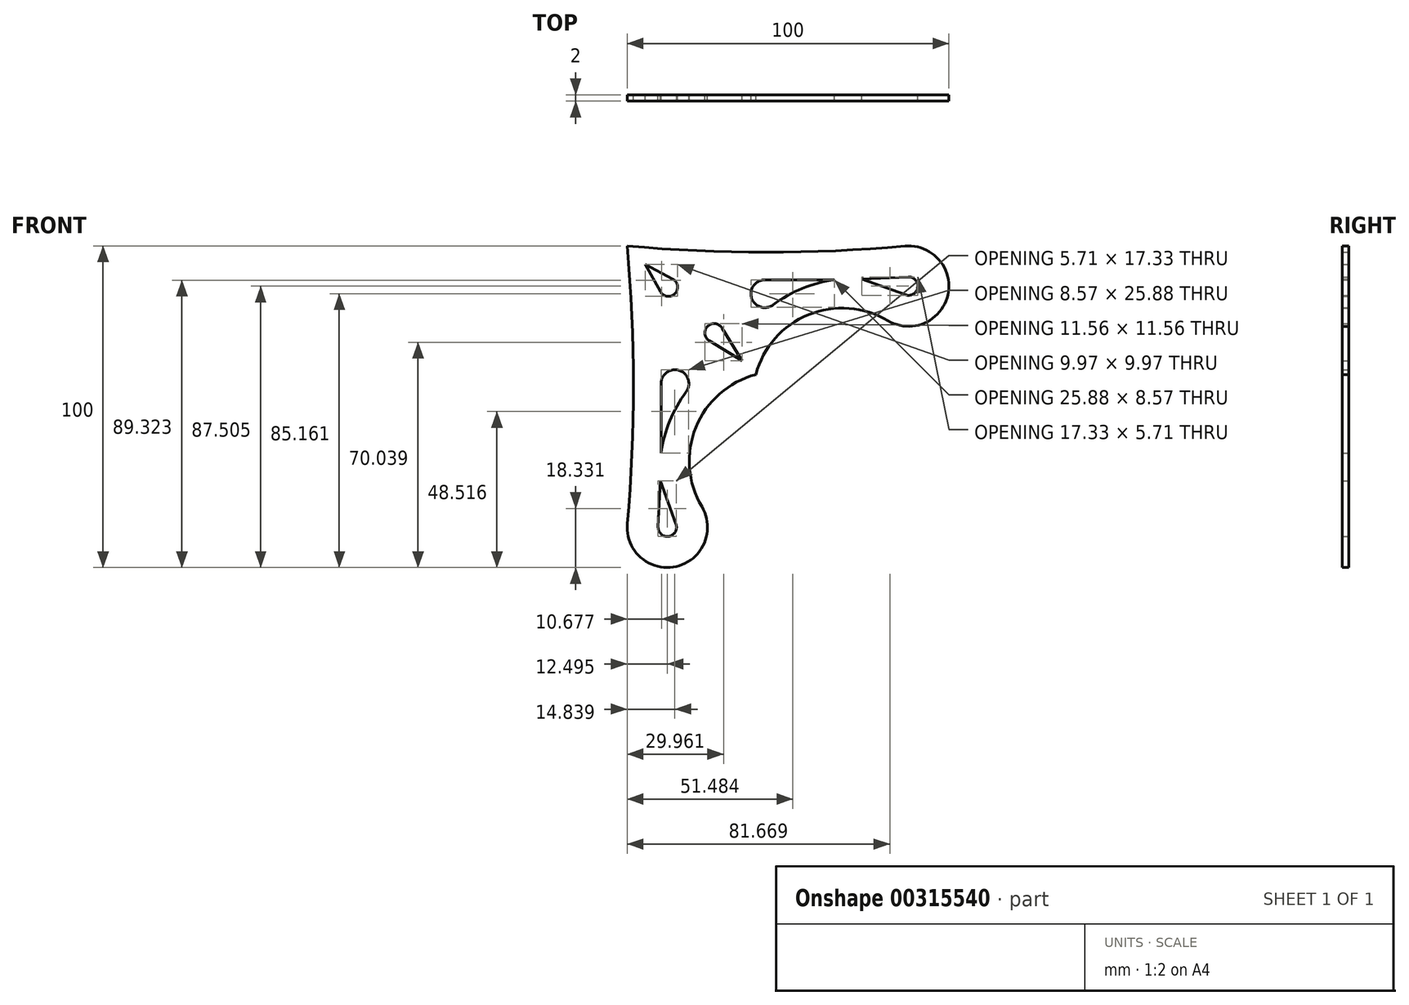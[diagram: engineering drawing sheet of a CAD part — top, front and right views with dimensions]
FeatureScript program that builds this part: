
annotation { "Feature Type Name" : "Feature", "Feature Type Description" : "" }
export const myFeature = defineFeature(function(context is Context, id is Id, definition is map)
    precondition{}
    {
        {
            var Q0;
            Q0=qCreatedBy(makeId("Front.planeOp"),FACE);
            var sketch = newSketch(context, id + "F0", { "sketchPlane" : qUnion([Q0])});
            skArc(sketch, "E0", {"start": v(0.05, -86.38) * mm, "mid": v(15.27, -99.69) * mm, "end": v(23.24, -81.1) * mm});
            skArc(sketch, "E1", {"start": v(40, -40) * mm, "mid": v(21.38, -56.38) * mm, "end": v(23.24, -81.1) * mm});
            skPoint(sketch, "E2.orphan", {"position": v(0, -100) * mm});
            skArc(sketch, "E3", {"start": v(0.05, -86.38) * mm, "mid": v(1.98, -43.19) * mm, "end": v(0, 0) * mm});
            skArc(sketch, "E4", {"start": v(9.64, -87.37) * mm, "mid": v(12.93, -90.33) * mm, "end": v(15.2, -86.53) * mm});
            skLineSegment(sketch, "E5", {"start": v(9.64, -87.37) * mm, "end": v(10.3, -73) * mm});
            skLineSegment(sketch, "E6", {"start": v(10.3, -73) * mm, "end": v(15.2, -86.53) * mm});
            skArc(sketch, "E7", {"start": v(10.29, -14.18) * mm, "mid": v(12.4, -15.66) * mm, "end": v(14.85, -14.85) * mm});
            skLineSegment(sketch, "E8", {"start": v(10.29, -14.18) * mm, "end": v(5.7, -5.7) * mm});
            skArc(sketch, "E9", {"start": v(25, -25) * mm, "mid": v(24.18, -27.4) * mm, "end": v(25.54, -29.52) * mm});
            skLineSegment(sketch, "E10", {"start": v(25.54, -29.52) * mm, "end": v(35.74, -35.74) * mm});
            skArc(sketch, "E11", {"start": v(18.33, -45.4) * mm, "mid": v(16.23, -38.72) * mm, "end": v(10.55, -42.81) * mm});
            skLineSegment(sketch, "E12", {"start": v(10.55, -42.81) * mm, "end": v(10.55, -64.42) * mm});
            skArc(sketch, "E13", {"start": v(18.33, -45.4) * mm, "mid": v(13.23, -54.41) * mm, "end": v(10.55, -64.42) * mm});
            skArc(sketch, "E14.MirrorCS", {"start": v(14.18, -10.29) * mm, "mid": v(15.66, -12.4) * mm, "end": v(14.85, -14.85) * mm});
            skArc(sketch, "E15.MirrorCS", {"start": v(25, -25) * mm, "mid": v(27.4, -24.18) * mm, "end": v(29.52, -25.54) * mm});
            skLineSegment(sketch, "E16.MirrorCS", {"start": v(29.52, -25.54) * mm, "end": v(35.74, -35.74) * mm});
            skLineSegment(sketch, "E17.MirrorCS", {"start": v(73, -10.3) * mm, "end": v(86.53, -15.2) * mm});
            skArc(sketch, "E18.MirrorCS", {"start": v(45.4, -18.33) * mm, "mid": v(54.41, -13.23) * mm, "end": v(64.42, -10.55) * mm});
            skLineSegment(sketch, "E19.MirrorCS", {"start": v(14.18, -10.29) * mm, "end": v(5.7, -5.7) * mm});
            skPoint(sketch, "E20.MirrorP", {"position": v(100, 0) * mm});
            skArc(sketch, "E21.MirrorCS", {"start": v(40, -40) * mm, "mid": v(56.38, -21.38) * mm, "end": v(81.1, -23.24) * mm});
            skArc(sketch, "E22.MirrorCS", {"start": v(45.4, -18.33) * mm, "mid": v(38.72, -16.23) * mm, "end": v(42.81, -10.55) * mm});
            skArc(sketch, "E23.MirrorCS", {"start": v(86.38, -0.05) * mm, "mid": v(43.19, -1.98) * mm, "end": v(0, 0) * mm});
            skArc(sketch, "E24.MirrorCS", {"start": v(86.38, -0.05) * mm, "mid": v(99.69, -15.27) * mm, "end": v(81.1, -23.24) * mm});
            skLineSegment(sketch, "E25.MirrorCS", {"start": v(42.81, -10.55) * mm, "end": v(64.42, -10.55) * mm});
            skLineSegment(sketch, "E26.MirrorCS", {"start": v(87.37, -9.64) * mm, "end": v(73, -10.3) * mm});
            skArc(sketch, "E27.MirrorCS", {"start": v(87.37, -9.64) * mm, "mid": v(90.33, -12.93) * mm, "end": v(86.53, -15.2) * mm});
            skSolve(sketch);
        }
        {
            var Q0;
            Q0=makeQuery(id+"F0.imprint","IMPRINT",FACE,{"disambiguationData":[TD([[makeQuery(id+"F0.imprint","IMPRINT",EDGE,{"derivedFrom":sQuery(id+"F0.wireOp",EDGE,"E0")}),1.0]])]});
            extrude(context, id + "F1", {"entities" : qUnion([Q0]), "depth" : 2 * mm});
        }
    });
